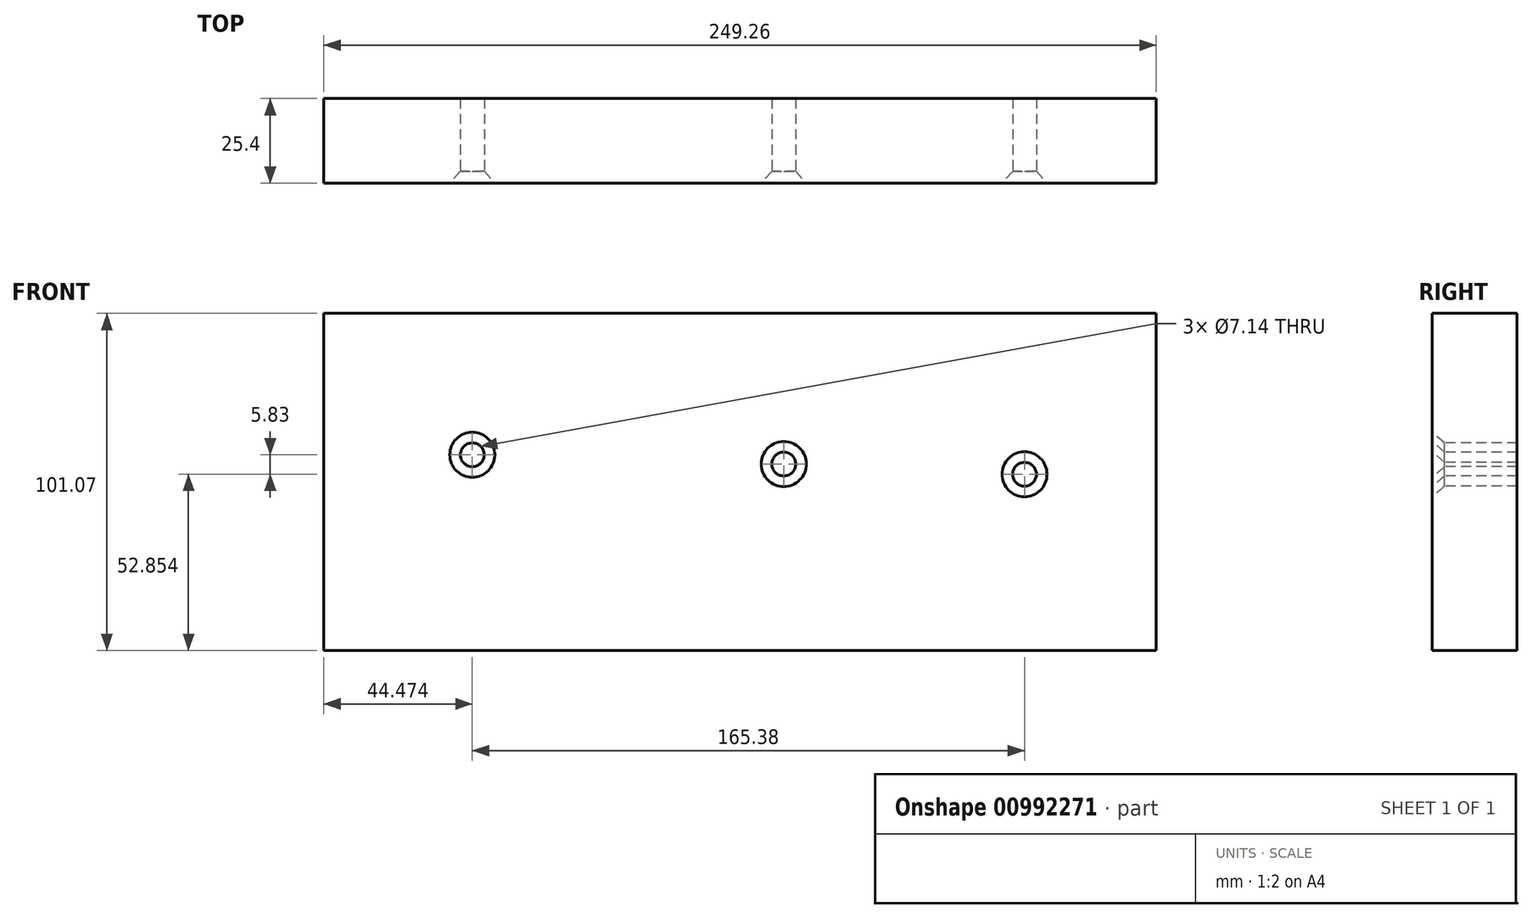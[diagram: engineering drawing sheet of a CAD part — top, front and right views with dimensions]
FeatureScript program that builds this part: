
annotation { "Feature Type Name" : "Feature", "Feature Type Description" : "" }
export const myFeature = defineFeature(function(context is Context, id is Id, definition is map)
    precondition{}
    {
        {
            var Q0;
            Q0=qCreatedBy(makeId("Front.planeOp"),FACE);
            var sketch = newSketch(context, id + "F0", { "sketchPlane" : qUnion([Q0])});
            skLineSegment(sketch, "E0.bottom", {"start": v(123.03, 36.94) * mm, "end": v(-126.23, 36.94) * mm});
            skLineSegment(sketch, "E0.top", {"start": v(123.03, -64.13) * mm, "end": v(-126.23, -64.13) * mm});
            skLineSegment(sketch, "E0.left", {"start": v(123.03, 36.94) * mm, "end": v(123.03, -64.13) * mm});
            skLineSegment(sketch, "E0.right", {"start": v(-126.23, 36.94) * mm, "end": v(-126.23, -64.13) * mm});
            skSolve(sketch);
        }
        {
            var Q0;
            Q0=makeQuery(id+"F0.imprint","IMPRINT",FACE,{"disambiguationData":[TD([[makeQuery(id+"F0.imprint","IMPRINT",EDGE,{"derivedFrom":sQuery(id+"F0.wireOp",EDGE,"E0.bottom")}),1.0]])]});
            extrude(context, id + "F1", {"entities" : qUnion([Q0]), "oppositeDirection" : true, "depth" : 25.4 * mm, "offsetDistance" : 25.4 * mm});
        }
        {
            var Q0;
            Q0=makeQuery(id+"F1.opExtrude","CAP_FACE",FACE,{"disambiguationData":[OSD([sQuery(id+"F0.wireOp",EDGE,"E0.bottom"),sQuery(id+"F0.wireOp",EDGE,"E0.top"),sQuery(id+"F0.wireOp",EDGE,"E0.left"),sQuery(id+"F0.wireOp",EDGE,"E0.right")])],"isStart":true});
            var sketch = newSketch(context, id + "F2", { "sketchPlane" : qUnion([Q0])});
            skPoint(sketch, "E1", {"position": v(-81.76, -5.45) * mm});
            skPoint(sketch, "E2", {"position": v(11.52, -8.2) * mm});
            skPoint(sketch, "E3", {"position": v(83.62, -11.28) * mm});
            skSolve(sketch);
        }
        {
            var Q0;
            Q0=sQuery(id+"F2.wireOp",VERTEX,"E1");
            var Q1;
            Q1=makeQuery(id+"F1.opExtrude","SWEPT_BODY",BODY,{"disambiguationData":[OSD([sQuery(id+"F0.wireOp",EDGE,"E0.bottom"),sQuery(id+"F0.wireOp",EDGE,"E0.top"),sQuery(id+"F0.wireOp",EDGE,"E0.left"),sQuery(id+"F0.wireOp",EDGE,"E0.right")])]});
            hole(context, id + "F3", {"style" : HoleStyle.C_SINK, "endStyle" : HoleEndStyle.THROUGH, "standardTappedOrClearance" : lookupTablePath({ "fit" : "Normal (ASME)", "standard" : "ANSI", "size" : "1/4", "type" : "Clearance" }), "standardBlindInLast" : lookupTablePath({ "fit" : "Normal", "standard" : "ANSI", "engagement" : "75%", "pitch" : "20 tpi", "size" : "1/4", "type" : "Clearance & tapped" }), "holeDiameter" : 7.14 * mm, "cSinkDiameter" : 13.5 * mm, "cSinkAngle" : 82 * degree, "majorDiameter" : 6.35 * mm, "isTappedThrough" : true, "tappedDepth" : 12.7 * mm, "tapClearance" : 3, "startFromSketch" : true, "locations" : qUnion([Q0]), "scope" : qUnion([Q1])});
        }
        {
            var Q0;
            Q0=sQuery(id+"F2.wireOp",VERTEX,"E2");
            var Q1;
            Q1=sQuery(id+"F2.wireOp",VERTEX,"E3");
            var Q2;
            Q2=makeQuery(id+"F1.opExtrude","SWEPT_BODY",BODY,{"disambiguationData":[OSD([sQuery(id+"F0.wireOp",EDGE,"E0.bottom"),sQuery(id+"F0.wireOp",EDGE,"E0.top"),sQuery(id+"F0.wireOp",EDGE,"E0.left"),sQuery(id+"F0.wireOp",EDGE,"E0.right")])]});
            hole(context, id + "F4", {"style" : HoleStyle.C_SINK, "endStyle" : HoleEndStyle.THROUGH, "standardTappedOrClearance" : lookupTablePath({ "fit" : "Normal (ASME)", "standard" : "ANSI", "size" : "1/4", "type" : "Clearance" }), "standardBlindInLast" : lookupTablePath({ "fit" : "Normal", "standard" : "ANSI", "engagement" : "75%", "pitch" : "20 tpi", "size" : "1/4", "type" : "Clearance & tapped" }), "holeDiameter" : 7.14 * mm, "cSinkDiameter" : 13.5 * mm, "cSinkAngle" : 82 * degree, "majorDiameter" : 6.35 * mm, "isTappedThrough" : true, "tappedDepth" : 12.7 * mm, "tapClearance" : 3, "startFromSketch" : true, "locations" : qUnion([Q0, Q1]), "scope" : qUnion([Q2])});
        }
    });
